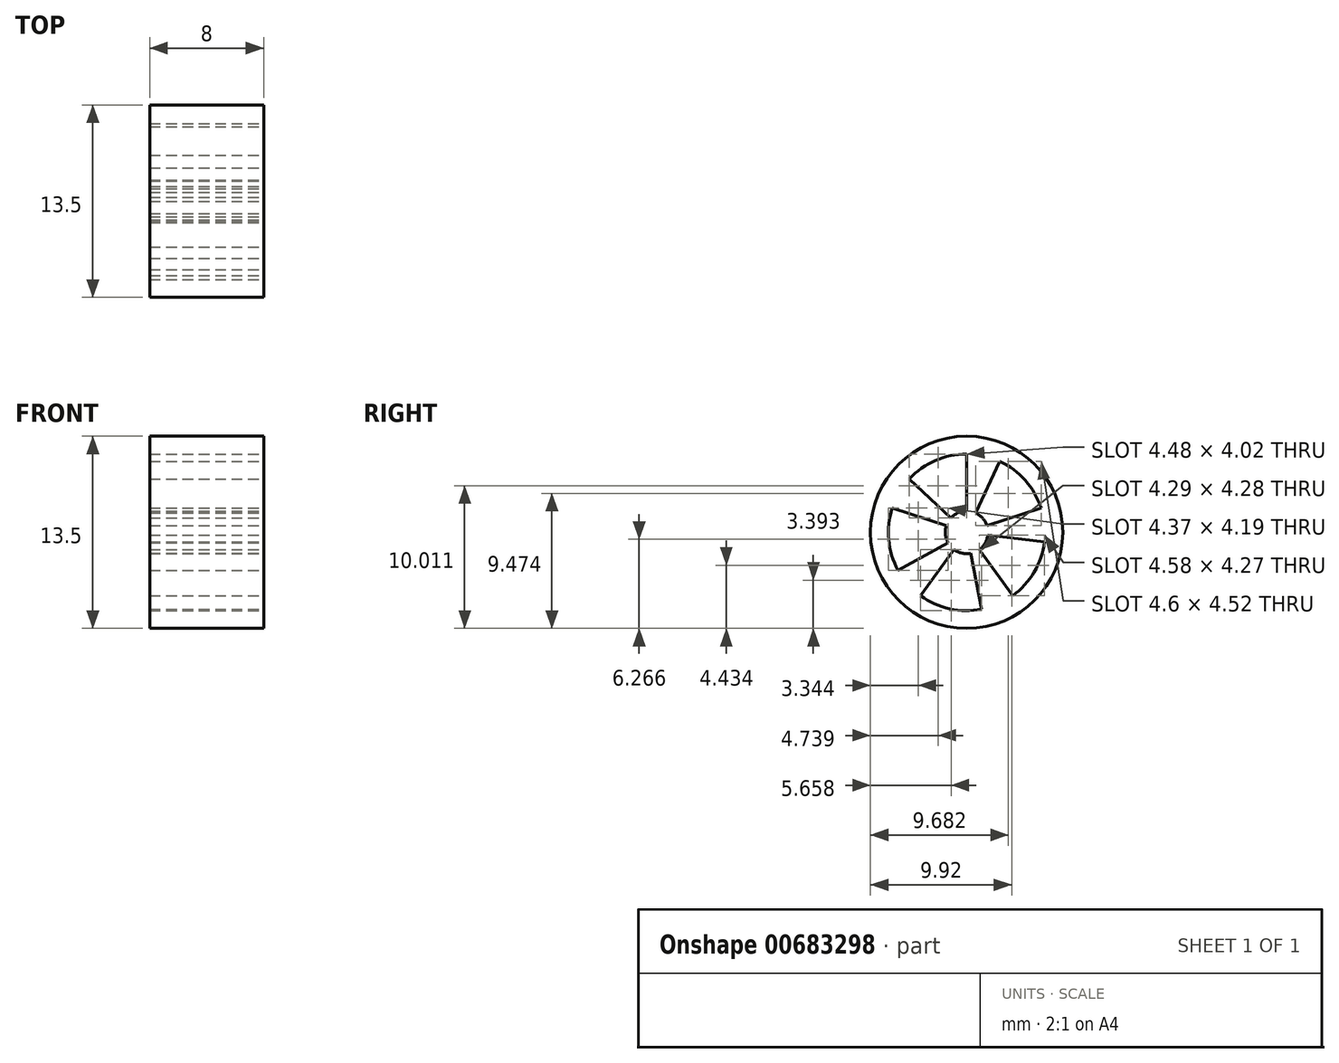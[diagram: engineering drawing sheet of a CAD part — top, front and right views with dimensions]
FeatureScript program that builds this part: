
annotation { "Feature Type Name" : "Feature", "Feature Type Description" : "" }
export const myFeature = defineFeature(function(context is Context, id is Id, definition is map)
    precondition{}
    {
        {
            var Q0;
            Q0=qCreatedBy(makeId("Right.planeOp"),FACE);
            var sketch = newSketch(context, id + "F0", { "sketchPlane" : qUnion([Q0])});
            skCircle(sketch, "E0", {"center": v(0, 0) * mm, "radius": 6.75 * mm});
            skSolve(sketch);
        }
        {
            var Q0;
            Q0 = qSketchRegion(id + "F0", true);
            extrude(context, id + "F1", {"entities" : qUnion([Q0]), "endBound" : BoundingType.SYMMETRIC, "depth" : 8 * mm, "offsetDistance" : 25 * mm});
        }
        {
            var Q0;
            Q0=makeQuery(id+"F1.opExtrude","CAP_FACE",FACE,{"disambiguationData":[OSD([sQuery(id+"F0.wireOp",EDGE,"E0")])],"isStart":false});
            var sketch = newSketch(context, id + "F2", { "sketchPlane" : qUnion([Q0])});
            skCircle(sketch, "E1", {"center": v(0, 0) * mm, "radius": 1.5 * mm});
            skCircle(sketch, "E2", {"center": v(0, 0) * mm, "radius": 5.5 * mm});
            skLineSegment(sketch, "E3", {"start": v(0, 1.5) * mm, "end": v(0, 5.5) * mm});
            skLineSegment(sketch, "E4", {"start": v(0.63, 1.36) * mm, "end": v(2.32, 4.98) * mm});
            skLineSegment(sketch, "E5.1.0", {"start": v(-1.43, 0.46) * mm, "end": v(-5.23, 1.7) * mm});
            skLineSegment(sketch, "E5.1.1", {"start": v(-1.1, 1.02) * mm, "end": v(-4.02, 3.75) * mm});
            skLineSegment(sketch, "E5.2.0", {"start": v(-0.88, -1.21) * mm, "end": v(-3.23, -4.45) * mm});
            skLineSegment(sketch, "E5.2.1", {"start": v(-1.31, -0.73) * mm, "end": v(-4.81, -2.67) * mm});
            skLineSegment(sketch, "E5.3.0", {"start": v(0.88, -1.21) * mm, "end": v(3.23, -4.45) * mm});
            skLineSegment(sketch, "E5.3.1", {"start": v(0.29, -1.47) * mm, "end": v(1.05, -5.4) * mm});
            skLineSegment(sketch, "E5.4.0", {"start": v(1.43, 0.46) * mm, "end": v(5.23, 1.7) * mm});
            skLineSegment(sketch, "E5.4.1", {"start": v(1.49, -0.18) * mm, "end": v(5.46, -0.67) * mm});
            skSolve(sketch);
        }
        {
            var Q0;
            {var subQ0=sQuery(id+"F2.wireOp",EDGE,"E3");Q0=makeQuery(id+"F2.imprint","IMPRINT",FACE,{"disambiguationData":[TD([[makeQuery(id+"F2.imprint","IMPRINT",EDGE,{"derivedFrom":subQ0}),1.0]])]});}
            var Q1;
            {var subQ0=sQuery(id+"F2.wireOp",EDGE,"E4");Q1=makeQuery(id+"F2.imprint","IMPRINT",FACE,{"disambiguationData":[TD([[makeQuery(id+"F2.imprint","IMPRINT",EDGE,{"derivedFrom":subQ0}),-1.0]])]});}
            var Q2;
            {var subQ0=sQuery(id+"F2.wireOp",EDGE,"E5.3.0");Q2=makeQuery(id+"F2.imprint","IMPRINT",FACE,{"disambiguationData":[TD([[makeQuery(id+"F2.imprint","IMPRINT",EDGE,{"derivedFrom":subQ0}),1.0]])]});}
            var Q3;
            {var subQ0=sQuery(id+"F2.wireOp",EDGE,"E5.2.0");Q3=makeQuery(id+"F2.imprint","IMPRINT",FACE,{"disambiguationData":[TD([[makeQuery(id+"F2.imprint","IMPRINT",EDGE,{"derivedFrom":subQ0}),1.0]])]});}
            var Q4;
            {var subQ0=sQuery(id+"F2.wireOp",EDGE,"E5.1.0");Q4=makeQuery(id+"F2.imprint","IMPRINT",FACE,{"disambiguationData":[TD([[makeQuery(id+"F2.imprint","IMPRINT",EDGE,{"derivedFrom":subQ0}),1.0]])]});}
            extrude(context, id + "F3", {"entities" : qUnion([Q0, Q1, Q2, Q3, Q4]), "operationType" : NewBodyOperationType.REMOVE, "endBound" : BoundingType.THROUGH_ALL, "oppositeDirection" : true, "depth" : 25 * mm, "offsetDistance" : 25 * mm});
        }
    });
